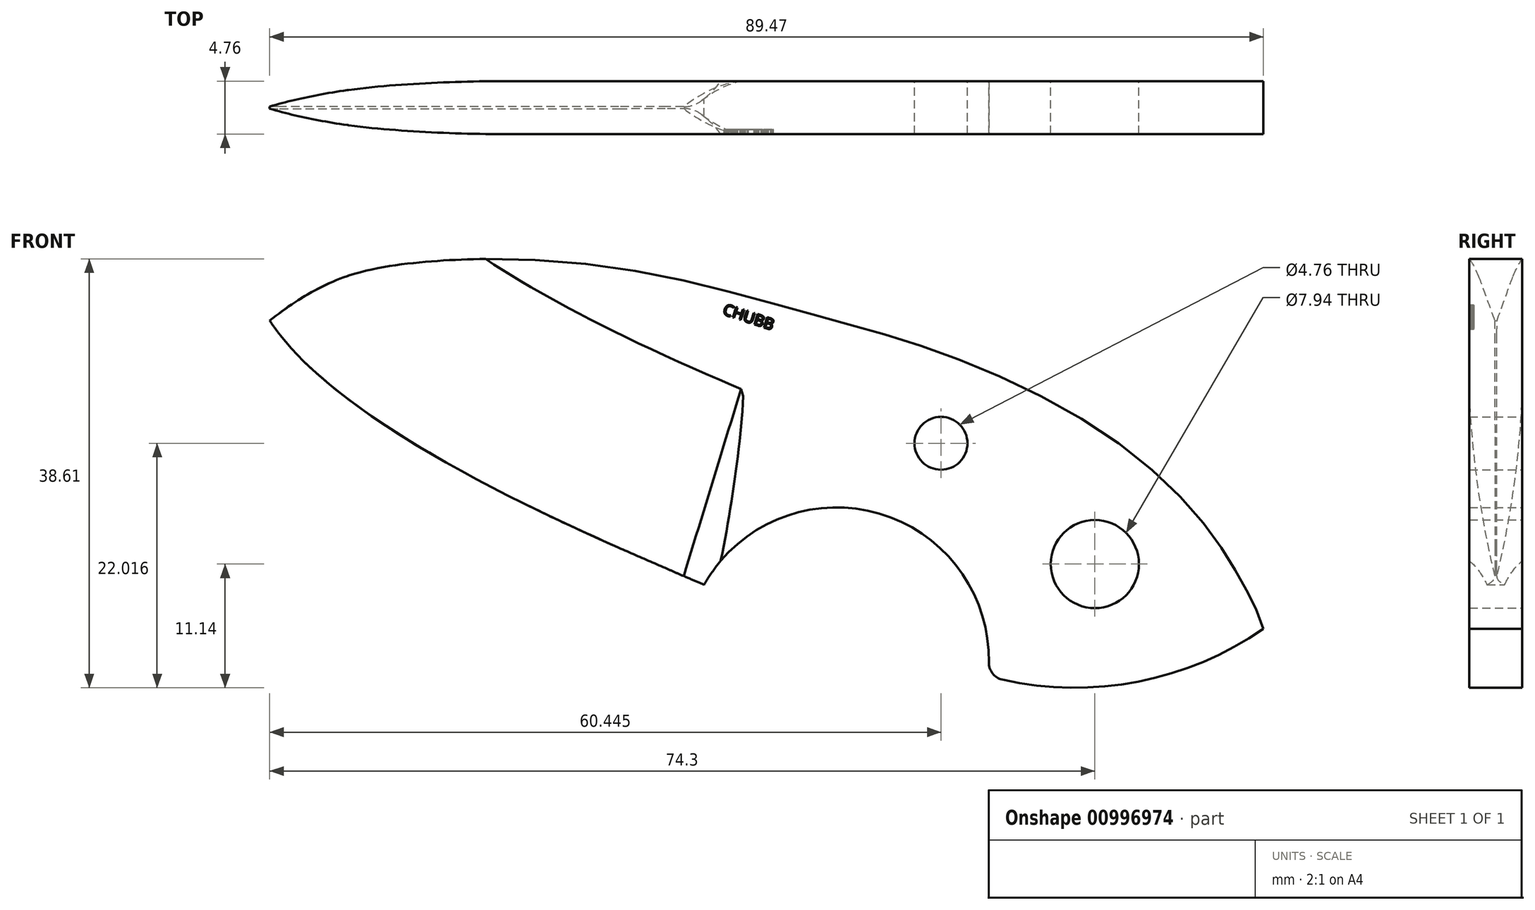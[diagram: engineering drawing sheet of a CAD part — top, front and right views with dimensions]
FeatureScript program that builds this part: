
annotation { "Feature Type Name" : "Feature", "Feature Type Description" : "" }
export const myFeature = defineFeature(function(context is Context, id is Id, definition is map)
    precondition{}
    {
        {
            var Q0;
            Q0=qCreatedBy(makeId("Front.planeOp"),FACE);
            var sketch = newSketch(context, id + "F0", { "sketchPlane" : qUnion([Q0])});
            skArc(sketch, "E0", {"start": v(20.85, -22.6) * mm, "mid": v(11.42, -8.07) * mm, "end": v(-4.7, -14.38) * mm});
            skFitSpline(sketch, "E1", {"points": [v(-4.7, -14.38) * mm, v(-27.5, -3.6) * mm, v(-43.82, 9.42) * mm, v(-46.86, 19.96) * mm], "startDerivative": vector(-59.32, 25.5) * mm, "endDerivative": vector(-4.82, 41.55) * mm});
            skFitSpline(sketch, "E2", {"points": [v(-43.82, 9.42) * mm, v(-32.7, 14.36) * mm, v(-13.42, 14.28) * mm, v(4.62, 10.08) * mm, v(16.57, 6.54) * mm, v(32.14, -1.3) * mm, v(41.12, -9.94) * mm, v(44.08, -14.8) * mm, v(45.65, -18.34) * mm, v(46.3, -23.78) * mm], "startDerivative": vector(108.84, 84.46) * mm, "endDerivative": vector(4.53, -74.76) * mm});
            skArc(sketch, "E3", {"start": v(20.85, -22.6) * mm, "mid": v(33.72, -23.22) * mm, "end": v(45.65, -18.34) * mm});
            skCircle(sketch, "E4", {"center": v(16.63, -1.63) * mm, "radius": 2.38 * mm});
            skCircle(sketch, "E5", {"center": v(30.48, -12.5) * mm, "radius": 3.97 * mm});
            skPoint(sketch, "E6", {"position": v(-7.9, -13) * mm});
            skLineSegment(sketch, "E7", {"start": v(-7.9, -13) * mm, "end": v(0, 11.36) * mm, "construction": true});
            skLineSegment(sketch, "E8", {"start": v(-4.7, -14.38) * mm, "end": v(5.06, 15.74) * mm, "construction": true});
            skArc(sketch, "E9", {"start": v(-8.02, -12.95) * mm, "mid": v(-9.25, -9.82) * mm, "end": v(-12.39, -11.04) * mm});
            skFitSpline(sketch, "E10.trimOffspring", {"points": [v(-4.7, -14.38) * mm, v(-27.5, -3.6) * mm, v(-43.82, 9.42) * mm, v(-46.86, 19.96) * mm], "startDerivative": vector(-59.32, 25.5) * mm, "endDerivative": vector(-4.82, 41.55) * mm});
            skSolve(sketch);
        }
        {
            var Q0;
            Q0 = qSketchRegion(id + "F0", true);
            extrude(context, id + "F1", {"entities" : qUnion([Q0]), "depth" : 4.76 * mm, "offsetDistance" : 25.4 * mm, "symmetric" : true});
        }
        {
            var Q0;
            Q0=qCreatedBy(makeId("Right.planeOp"),FACE);
            var sketch = newSketch(context, id + "F2", { "sketchPlane" : qUnion([Q0])});
            skLineSegment(sketch, "E11", {"start": v(-10.98, 0) * mm, "end": v(69.03, 0) * mm, "construction": true});
            skSolve(sketch);
        }
        {
            var Q0;
            Q0=qCreatedBy(makeId("Right.planeOp"),FACE);
            var Q1;
            Q1=sQuery(id+"F2.wireOp",EDGE,"E11");
            cPlane(context, id + "F3", {"entities" : qUnion([Q0, Q1]), "cplaneType" : CPlaneType.LINE_ANGLE, "offset" : 25.4 * mm, "angle" : 17 * degree, "width" : 152.4 * mm, "height" : 152.4 * mm});
        }
        {
            var Q0;
            Q0=qCreatedBy(id+"F3.planeOp",FACE);
            cPlane(context, id + "F4", {"entities" : qUnion([Q0]), "cplaneType" : CPlaneType.OFFSET, "offset" : 3.43 * mm, "width" : 152.4 * mm, "height" : 152.4 * mm});
        }
        {
            var Q0;
            Q0=qCreatedBy(id+"F4.planeOp",FACE);
            var sketch = newSketch(context, id + "F5", { "sketchPlane" : qUnion([Q0])});
            skLineSegment(sketch, "E12.0", {"start": v(2.38, -15.12) * mm, "end": v(-2.38, -15.12) * mm, "construction": true});
            skFitSpline(sketch, "E13.0", {"points": [v(2.38, -15.12) * mm, v(2.38, -14.2) * mm, v(2.38, -12.46) * mm, v(2.38, -5.7) * mm, v(2.38, 2.1) * mm, v(2.38, 5.4) * mm], "construction": true});
            skLineSegment(sketch, "E14", {"start": v(2.38, -3.8) * mm, "end": v(2.38, 5.02) * mm, "construction": true});
            skLineSegment(sketch, "E15", {"start": v(-2.38, -15.12) * mm, "end": v(-2.38, 2.84) * mm, "construction": true});
            skLineSegment(sketch, "E16", {"start": v(-2.38, 2.84) * mm, "end": v(-4.93, 2.84) * mm});
            skLineSegment(sketch, "E17", {"start": v(-4.93, 2.84) * mm, "end": v(-4.93, -16.65) * mm});
            skLineSegment(sketch, "E18", {"start": v(-4.93, -16.65) * mm, "end": v(5.84, -16.65) * mm});
            skLineSegment(sketch, "E19", {"start": v(5.84, -16.65) * mm, "end": v(5.84, 2.84) * mm});
            skLineSegment(sketch, "E20", {"start": v(5.84, 2.84) * mm, "end": v(2.38, 2.84) * mm});
            skArc(sketch, "E21", {"start": v(0, -15.12) * mm, "mid": v(1.63, -6.2) * mm, "end": v(2.38, 2.84) * mm});
            skArc(sketch, "E22.MirrorCS", {"start": v(0, -15.12) * mm, "mid": v(-1.63, -6.2) * mm, "end": v(-2.38, 2.84) * mm});
            skSolve(sketch);
        }
        {
            var Q0;
            Q0=makeQuery(id+"F1.opExtrude","CAP_FACE",FACE,{"disambiguationData":[OSD([sQuery(id+"F0.wireOp",EDGE,"E0"),sQuery(id+"F0.wireOp",EDGE,"E1"),sQuery(id+"F0.wireOp",EDGE,"E2"),sQuery(id+"F0.wireOp",EDGE,"E3"),sQuery(id+"F0.wireOp",EDGE,"E4"),sQuery(id+"F0.wireOp",EDGE,"E5")])],"isStart":false});
            var sketch = newSketch(context, id + "F6", { "sketchPlane" : qUnion([Q0])});
            skFitSpline(sketch, "E23.0", {"points": [v(-4.7, -14.23) * mm, v(-12.4, -10.92) * mm, v(-27.1, -4.6) * mm, v(-45.47, 8.1) * mm, v(-46.45, 16.55) * mm, v(-46.86, 20.1) * mm], "construction": true});
            skFitSpline(sketch, "E24.0", {"points": [v(-0.32, -4.02) * mm, v(-2.79, -2.96) * mm, v(-7.66, -0.87) * mm, v(-13.5, 1.8) * mm, v(-18.03, 4.05) * mm, v(-21.33, 5.8) * mm, v(-24.56, 7.66) * mm, v(-27.56, 9.55) * mm, v(-29.77, 11.11) * mm, v(-31.3, 12.31) * mm, v(-32.3, 13.17) * mm, v(-33.13, 13.98) * mm, v(-33.68, 14.57) * mm, v(-34.04, 14.99) * mm, v(-34.25, 15.26) * mm, v(-34.42, 15.5) * mm, v(-34.54, 15.68) * mm, v(-34.65, 15.87) * mm, v(-34.78, 16.1) * mm, v(-34.92, 16.43) * mm, v(-35.08, 16.9) * mm, v(-35.24, 17.48) * mm, v(-35.4, 18.21) * mm, v(-35.59, 19.4) * mm, v(-35.72, 20.52) * mm, v(-35.82, 21.39) * mm]});
            skLineSegment(sketch, "E25", {"start": v(-7.6, -13.13) * mm, "end": v(-4.33, -2.44) * mm, "construction": true});
            skCircle(sketch, "E26", {"center": v(16.63, -1.63) * mm, "radius": 2.38 * mm, "construction": true});
            skFitSpline(sketch, "E27", {"points": [v(-43.82, 9.56) * mm, v(-39.61, 12.82) * mm, v(-33.3, 15.23) * mm, v(-13.08, 15.42) * mm, v(4.57, 10.1) * mm, v(16.52, 7.2) * mm, v(32.49, -0.18) * mm, v(41.2, -9.24) * mm, v(44.02, -14.56) * mm, v(45.98, -18.13) * mm, v(46.2, -21.7) * mm, v(46.3, -23.64) * mm], "construction": true});
            skFitSpline(sketch, "E28", {"points": [v(-4.7, -14.23) * mm, v(-12.4, -10.92) * mm, v(-27.1, -4.6) * mm, v(-45.47, 8.1) * mm, v(-46.45, 16.55) * mm, v(-46.86, 20.1) * mm], "construction": true});
            skPoint(sketch, "E29.orphan", {"position": v(-4.7, -14.38) * mm});
            skLineSegment(sketch, "E30", {"start": v(-38.62, 26.83) * mm, "end": v(-57.55, 15.48) * mm, "construction": true});
            skSolve(sketch);
        }
        {
            var Q0;
            Q0 = qSketchRegion(id + "F5", true);
            var Q1;
            Q1=sQuery(id+"F6.wireOp",EDGE,"E24.0");
            sweep(context, id + "F7", {"operationType" : NewBodyOperationType.REMOVE, "profiles" : qUnion([Q0]), "path" : qUnion([Q1])});
        }
        {
            var Q0;
            Q0=makeQuery(id+"F7.boolean.opBoolean","COPY",EDGE,{"derivedFrom":makeQuery(id+"F7.opSweep","CAP_EDGE",EDGE,{"disambiguationData":[OSD([sQuery(id+"F5.wireOp",EDGE,"j4xr096f-cLiE-1jE8-ExDm-pdsodM7f9Gvq"),sQuery(id+"F6.wireOp",VERTEX,"E24.0.start")])],"isStart":true})});
            var Q1;
            Q1=makeQuery(id+"F7.boolean.opBoolean","COPY",EDGE,{"derivedFrom":makeQuery(id+"F7.opSweep","CAP_EDGE",EDGE,{"disambiguationData":[OSD([sQuery(id+"F5.wireOp",EDGE,"mgjF08Ri-qkRh-4gWA-V68d-xkGMz0zFTvxb"),sQuery(id+"F6.wireOp",VERTEX,"E24.0.start")])],"isStart":true})});
            fillet(context, id + "F8", {"entities" : qUnion([Q0, Q1]), "radius" : 3.17 * mm, "tangentPropagation" : true, "allowEdgeOverflow" : false});
        }
        {
            var Q0;
            Q0=qCreatedBy(makeId("Top.planeOp"),FACE);
            var sketch = newSketch(context, id + "F9", { "sketchPlane" : qUnion([Q0])});
            skFitSpline(sketch, "E31.0", {"points": [v(-5.29, -2.38) * mm, v(-11.63, -2.38) * mm, v(-17.97, -2.38) * mm, v(-24.31, -2.38) * mm]});
            skFitSpline(sketch, "E32", {"points": [v(-9.3, -2.38) * mm, v(-9.99, -2.05) * mm, v(-11.13, -2.08) * mm, v(-11.5, -2.2) * mm, v(-11.95, -2.38) * mm, v(-12.32, -2.23) * mm, v(-12.6, -2.13) * mm, v(-13.3, -2.38) * mm, v(-14.06, -2.19) * mm, v(-15.1, -2.03) * mm, v(-15.3, -1.95) * mm, v(-16.29, -2) * mm, v(-17.05, -2.38) * mm, v(-17.71, -2.18) * mm, v(-17.91, -2.1) * mm, v(-18.3, -1.98) * mm, v(-19.24, -2.38) * mm, v(-20.42, -2.02) * mm, v(-20.88, -2.06) * mm, v(-21.4, -2.38) * mm, v(-21.87, -2.26) * mm, v(-22.32, -2.38) * mm, v(-22.79, -2.23) * mm, v(-23.07, -2.38) * mm, v(-22.17, -3.77) * mm, v(-9.3, -2.38) * mm]});
            skFitSpline(sketch, "E33", {"points": [v(-11.95, -2.38) * mm, v(-11.52, -2.24) * mm, v(-11.4, -2.22) * mm, v(-11.04, -2.2) * mm, v(-10.58, -2.38) * mm, v(-10.08, -2.2) * mm, v(-9.97, -2.2) * mm, v(-9.48, -2.38) * mm, v(-9.42, -2.35) * mm, v(-8.96, -2.25) * mm, v(-8.86, -2.25) * mm, v(-8.59, -2.38) * mm, v(-8.2, -2.27) * mm, v(-7.95, -2.38) * mm, v(-7.76, -2.73) * mm, v(-9.75, -3.56) * mm, v(-10.17, -3.63) * mm, v(-24.52, -2.99) * mm, v(-24.32, -2.38) * mm, v(-24.12, -2.27) * mm, v(-24.06, -2.28) * mm, v(-23.88, -2.33) * mm, v(-23.78, -2.32) * mm, v(-23.6, -2.25) * mm, v(-23.5, -2.27) * mm, v(-23.29, -2.35) * mm, v(-23.07, -2.38) * mm], "startDerivative": vector(13.18, 4.6) * mm, "endDerivative": vector(8.02, -0.9) * mm});
            skFitSpline(sketch, "E34.0", {"points": [v(-5.29, 2.38) * mm, v(-11.63, 2.38) * mm, v(-17.97, 2.38) * mm, v(-24.31, 2.38) * mm], "construction": true});
            skFitSpline(sketch, "E35", {"points": [v(-24.32, 2.38) * mm, v(-23.59, 2.07) * mm, v(-22.89, 2.13) * mm, v(-22.57, 2.38) * mm, v(-21.83, 2.15) * mm, v(-21.53, 2.1) * mm, v(-21.31, 2.07) * mm, v(-20.86, 2.38) * mm, v(-20.26, 2.38) * mm, v(-19.74, 2.07) * mm, v(-19.44, 1.93) * mm, v(-19.08, 1.9) * mm, v(-18.3, 2.01) * mm, v(-17.73, 2.2) * mm, v(-17.37, 2.21) * mm, v(-16.57, 2.11) * mm, v(-16.13, 2.07) * mm, v(-15.11, 2.38) * mm, v(-14.42, 2.21) * mm, v(-14, 2.07) * mm, v(-13.62, 2.1) * mm, v(-12.92, 2.38) * mm, v(-12.18, 2.13) * mm, v(-11.85, 2.05) * mm, v(-11.35, 2.03) * mm, v(-10.87, 2.05) * mm, v(-10.47, 2.15) * mm, v(-9.83, 2.38) * mm, v(-8.88, 2.07) * mm, v(-8.54, 2.38) * mm, v(-7.82, 2.38) * mm, v(-7.34, 2.7) * mm, v(-7.28, 3.05) * mm, v(-7.54, 3.2) * mm, v(-8.22, 3.5) * mm, v(-9.31, 3.86) * mm, v(-11, 4.4) * mm, v(-13.26, 4.78) * mm, v(-16.67, 5.14) * mm, v(-19.24, 5.14) * mm, v(-20.58, 4.92) * mm, v(-21.91, 4.52) * mm, v(-24.32, 2.59) * mm, v(-24.32, 2.38) * mm]});
            skFitSpline(sketch, "E36", {"points": [v(-24.32, -2.38) * mm, v(-24.88, -2.1) * mm, v(-25, -2.1) * mm, v(-25.86, -2.08) * mm, v(-26.16, -2.07) * mm, v(-26.77, -1.94) * mm, v(-27.07, -1.86) * mm, v(-27.52, -1.96) * mm, v(-27.82, -1.98) * mm, v(-28.07, -1.96) * mm, v(-28.24, -1.95) * mm, v(-28.58, -1.97) * mm, v(-28.67, -1.97) * mm, v(-28.83, -1.9) * mm, v(-28.94, -1.85) * mm, v(-29.14, -1.89) * mm, v(-29.29, -1.96) * mm, v(-29.4, -1.97) * mm, v(-29.58, -1.92) * mm, v(-29.84, -1.75) * mm, v(-29.95, -1.72) * mm, v(-30.66, -1.81) * mm, v(-31.04, -1.87) * mm, v(-31.13, -1.82) * mm, v(-31.24, -1.73) * mm, v(-31.44, -1.64) * mm, v(-31.6, -1.57) * mm, v(-31.8, -1.55) * mm, v(-32, -1.64) * mm, v(-32.2, -1.7) * mm, v(-32.38, -1.67) * mm, v(-32.65, -1.56) * mm, v(-32.76, -1.51) * mm, v(-32.95, -1.49) * mm, v(-33.1, -1.52) * mm, v(-33.48, -1.42) * mm, v(-33.87, -1.33) * mm, v(-34.18, -1.29) * mm, v(-34.45, -1.37) * mm, v(-34.78, -1.48) * mm, v(-34.97, -1.43) * mm, v(-35.42, -1.14) * mm, v(-35.7, -1.1) * mm, v(-36.27, -1.1) * mm, v(-36.55, -1.2) * mm, v(-37.5, -0.87) * mm, v(-37.79, -0.89) * mm, v(-38.18, -1.02) * mm, v(-38.32, -1.06) * mm, v(-38.63, -1) * mm, v(-38.89, -0.84) * mm, v(-38.98, -0.76) * mm, v(-39.4, -0.72) * mm, v(-39.66, -0.8) * mm, v(-40.13, -0.85) * mm, v(-40.36, -0.76) * mm, v(-40.6, -0.63) * mm, v(-40.87, -0.6) * mm, v(-41.42, -0.59) * mm, v(-41.64, -0.5) * mm, v(-41.78, -0.41) * mm, v(-42.04, -0.31) * mm, v(-42.11, -0.3) * mm, v(-42.3, -0.31) * mm, v(-42.83, -0.18) * mm, v(-43.15, -0.26) * mm, v(-43.22, -0.24) * mm, v(-43.38, -0.1) * mm, v(-43.77, -0.18) * mm, v(-43.89, -0.18) * mm, v(-44.03, 0.07) * mm, v(-43.96, 0.12) * mm, v(-43.64, 0.26) * mm, v(-43.52, 0.23) * mm, v(-43.15, 0.15) * mm, v(-42.95, 0.14) * mm, v(-42.69, 0.31) * mm, v(-42.5, 0.36) * mm, v(-42.31, 0.3) * mm, v(-42.1, 0.28) * mm, v(-41.93, 0.28) * mm, v(-41.73, 0.34) * mm, v(-41.44, 0.44) * mm, v(-41.27, 0.47) * mm, v(-40.95, 0.45) * mm, v(-40.65, 0.48) * mm, v(-40.52, 0.58) * mm, v(-40.3, 0.73) * mm, v(-40.03, 0.77) * mm, v(-39.78, 0.68) * mm, v(-39.6, 0.58) * mm, v(-39.32, 0.6) * mm, v(-39.28, 0.65) * mm, v(-39.17, 0.77) * mm, v(-38.97, 0.89) * mm, v(-38.55, 0.95) * mm, v(-38.33, 1.02) * mm, v(-38.14, 1.07) * mm, v(-37.58, 0.96) * mm, v(-37.42, 0.95) * mm, v(-37.17, 0.97) * mm, v(-37, 0.99) * mm, v(-36.8, 1.08) * mm, v(-36.65, 1.2) * mm, v(-36.08, 1.31) * mm, v(-35.94, 1.16) * mm, v(-35.56, 1.25) * mm, v(-35.2, 1.22) * mm, v(-35.02, 1.23) * mm, v(-34.64, 1.4) * mm, v(-34.46, 1.4) * mm, v(-34.15, 1.4) * mm, v(-34, 1.35) * mm, v(-33.82, 1.36) * mm, v(-33.57, 1.37) * mm, v(-33.44, 1.43) * mm, v(-33.13, 1.57) * mm, v(-32.89, 1.63) * mm, v(-32.62, 1.64) * mm, v(-32.43, 1.6) * mm, v(-32.28, 1.55) * mm, v(-32.12, 1.54) * mm, v(-31.72, 1.63) * mm, v(-31.6, 1.66) * mm, v(-31.47, 1.67) * mm, v(-31.26, 1.66) * mm, v(-30.98, 1.65) * mm, v(-30.81, 1.69) * mm, v(-30.67, 1.78) * mm, v(-30.48, 1.82) * mm, v(-30.27, 1.83) * mm, v(-30, 1.8) * mm, v(-29.83, 1.83) * mm, v(-28.56, 2.11) * mm, v(-28.35, 2.19) * mm, v(-28.19, 2.3) * mm, v(-28.03, 2.43) * mm, v(-27.82, 2.58) * mm, v(-27.56, 2.57) * mm, v(-27.27, 2.46) * mm, v(-27.07, 2.38) * mm, v(-26.85, 2.34) * mm, v(-26.57, 2.4) * mm, v(-26.35, 2.52) * mm, v(-26.14, 2.58) * mm, v(-25.85, 2.58) * mm, v(-25.64, 2.51) * mm, v(-25.25, 2.48) * mm, v(-25.04, 2.48) * mm, v(-24.8, 2.7) * mm, v(-24.7, 2.71) * mm, v(-24.32, 2.38) * mm], "startDerivative": vector(-67.67, 35.6) * mm, "endDerivative": vector(49.8, -47.21) * mm});
            skFitSpline(sketch, "E37", {"points": [v(-7.82, 2.38) * mm, v(-7.65, 4.55) * mm, v(-8.41, 4.95) * mm, v(-10.67, 5.62) * mm, v(-12.61, 5.9) * mm, v(-14.38, 6.06) * mm, v(-16.82, 5.98) * mm, v(-26.27, 5.43) * mm, v(-28.82, 5.33) * mm, v(-33.4, 4.95) * mm, v(-35.67, 4.47) * mm, v(-39.28, 3.97) * mm, v(-41.51, 3.46) * mm, v(-43.95, 2.88) * mm, v(-45.1, 1.34) * mm, v(-46.12, -0.31) * mm, v(-45.26, -1.8) * mm, v(-43.05, -3.18) * mm, v(-38.39, -4.42) * mm, v(-31.49, -4.85) * mm, v(-26.77, -5.37) * mm, v(-17.06, -5.1) * mm, v(-14.77, -4.9) * mm, v(-8.99, -4.24) * mm, v(-8.67, -4) * mm, v(-8.07, -3.34) * mm, v(-8, -2.98) * mm, v(-7.95, -2.38) * mm], "startDerivative": vector(16.39, 79.9) * mm, "endDerivative": vector(5.04, 37.1) * mm});
            skSolve(sketch);
        }
        {
            var Q0;
            Q0=makeQuery(id+"F1.opExtrude","SWEPT_EDGE",EDGE,{"disambiguationData":[OSD([sQuery(id+"F0.wireOp",EDGE,"E0"),sQuery(id+"F0.wireOp",EDGE,"E3")])]});
            fillet(context, id + "F10", {"entities" : qUnion([Q0]), "radius" : 1.59 * mm, "tangentPropagation" : true, "defaultsChanged" : false, "vertexSettings" : [], "allowEdgeOverflow" : false});
        }
        {
            var Q0;
            {var subQ0=sQuery(id+"F0.wireOp",EDGE,"E2");var subQ1=sQuery(id+"F0.wireOp",EDGE,"E1");var subQ2=sQuery(id+"F5.wireOp",EDGE,"j4xr096f-cLiE-1jE8-ExDm-pdsodM7f9Gvq");var subQ3=sQuery(id+"F0.wireOp",EDGE,"E3");var subQ4=sQuery(id+"F0.wireOp",EDGE,"E0");var subQ5=sQuery(id+"F0.wireOp",EDGE,"E4");var subQ6=sQuery(id+"F0.wireOp",EDGE,"E5");Q0=makeQuery(id+"FRacjkfZQb5iDlf_1.boolean.opBoolean","SPLIT",FACE,{"disambiguationData":[TD([makeQuery(id+"F1.opExtrude","SWEPT_FACE",FACE,{"disambiguationData":[OSD([subQ4])]}),makeQuery(id+"F1.opExtrude","SWEPT_FACE",FACE,{"disambiguationData":[OSD([subQ1])]}),makeQuery(id+"F1.opExtrude","SWEPT_FACE",FACE,{"disambiguationData":[OSD([subQ0])]}),makeQuery(id+"F1.opExtrude","SWEPT_FACE",FACE,{"disambiguationData":[OSD([subQ3])]}),makeQuery(id+"F1.opExtrude","SWEPT_FACE",FACE,{"disambiguationData":[OSD([subQ5])]}),makeQuery(id+"F1.opExtrude","SWEPT_FACE",FACE,{"disambiguationData":[OSD([subQ6])]}),makeQuery(id+"F7.boolean.opBoolean","COPY",FACE,{"derivedFrom":makeQuery(id+"F7.opSweep","SWEPT_FACE",FACE,{"disambiguationData":[OSD([subQ2,sQuery(id+"F6.wireOp",EDGE,"E24.0")])]})}),makeQuery(id+"F8.opFillet","BLEND_FACE",FACE,{"disambiguationData":[OSD([subQ2,sQuery(id+"F6.wireOp",VERTEX,"E24.0.start")])]}),makeQuery(id+"FRacjkfZQb5iDlf_1.opExtrude","SWEPT_FACE",FACE,{"disambiguationData":[OSD([sQuery(id+"F9.wireOp",EDGE,"E33")])]})])],"derivedFrom":makeQuery(id+"F1.opExtrude","CAP_FACE",FACE,{"disambiguationData":[OSD([subQ4,subQ1,subQ0,subQ3,subQ5,subQ6,sQuery(id+"F0.wireOp",EDGE,"E9"),sQuery(id+"F0.wireOp",EDGE,"E10.trimOffspring")])],"isStart":false})});}
            var sketch = newSketch(context, id + "F11", { "sketchPlane" : qUnion([Q0])});
            skText(sketch, "E38", { "text": "CHUBB", "fontName": "OpenSans-Regular.ttf"});
            const initialGuessF11  = {"E38": [-0.00308, 0.01, 0.95119, -0.30862, 0.001]};
            skSetInitialGuess(sketch, initialGuessF11);
            skSolve(sketch);
        }
        {
            var Q0;
            Q0 = qSketchRegion(id + "F11", true);
            extrude(context, id + "F12", {"entities" : qUnion([Q0]), "operationType" : NewBodyOperationType.REMOVE, "oppositeDirection" : true, "depth" : 0.4 * mm, "offsetDistance" : 25.4 * mm});
        }
    });
